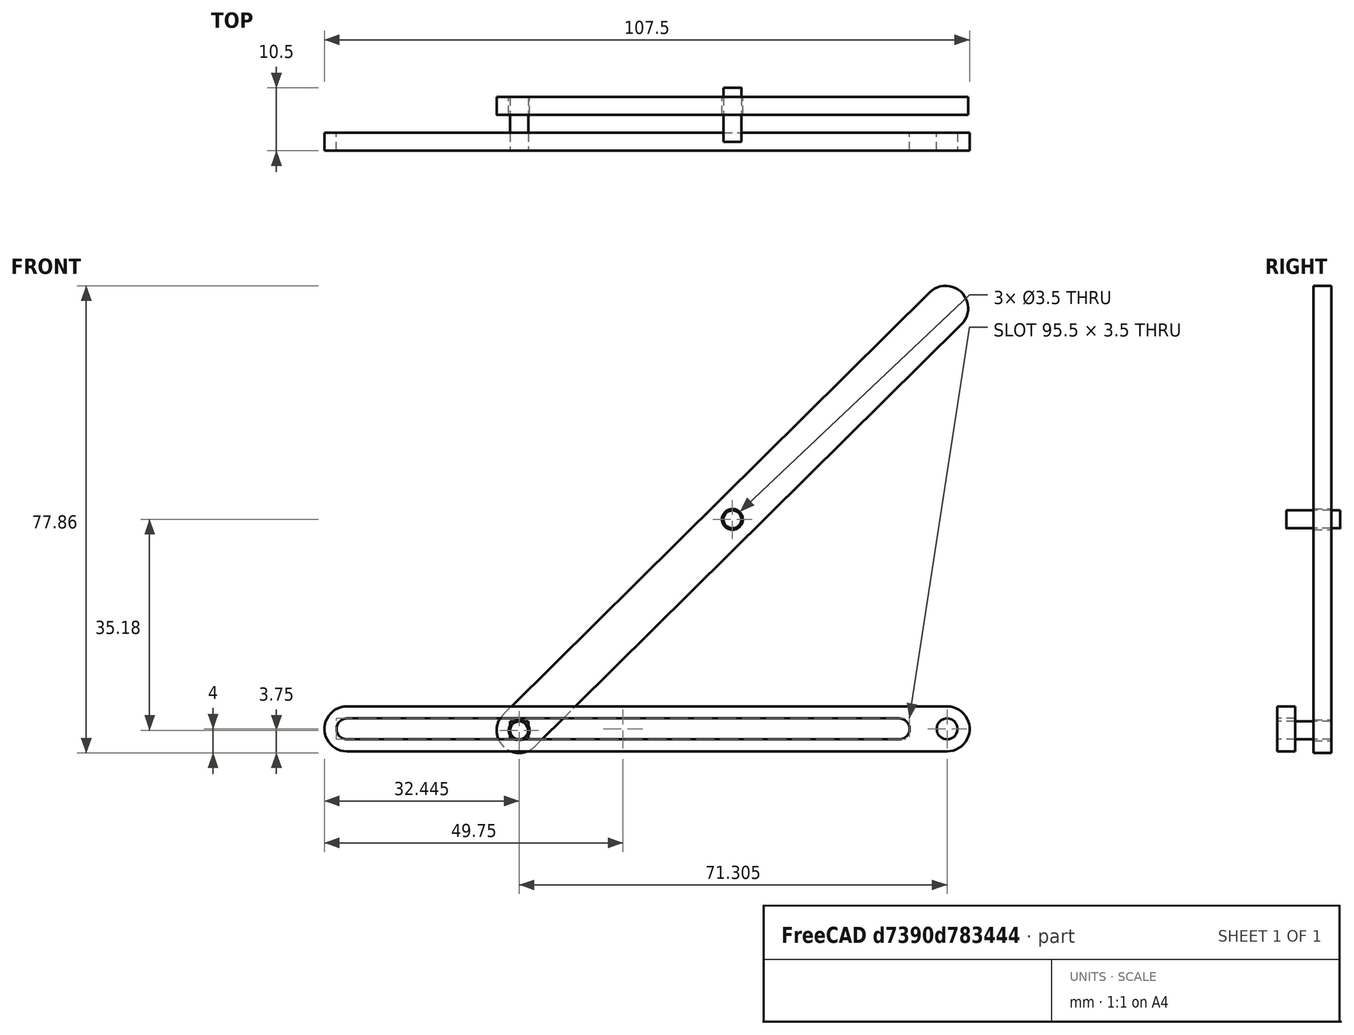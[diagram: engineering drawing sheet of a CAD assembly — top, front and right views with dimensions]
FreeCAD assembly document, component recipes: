
FREECAD ASSEMBLY — COMPONENT RECIPES ("scissor_lift")

This assembly document has 7 components, labeled P0..P6 below (a component is one placed body or linked part). 7 of them carry a construction recipe — the FreeCAD feature program that regenerates the part from scratch, quoted from this document or its linked companion documents; the rest are supplied as boundary geometry only. No exploded tour is included for this assembly.
COMPONENT P0 — recipe-attached ("base", modeled in this document).
Construction recipe (the document's own serialized feature program — sketch geometry with constraints, then the solid features built on it; lengths are millimeters unless a unit is written):

FEATURE [Sketcher::SketchObject] Sketch
  ArcFitTolerance = 1e-06
  AttachmentSupport = -> [XY_Plane]
  FullyConstrained = true
  MakeInternals = false
  MapMode = 5
  sketch-geometry (9):
    g0: ArcOfCircle CenterX=-50 CenterY=2e-16 CenterZ=0 NormalX=0 NormalY=0 NormalZ=1 AngleXU=0 Radius=3.75 StartAngle=1.5708 EndAngle=4.71239
    g1: ArcOfCircle CenterX=50 CenterY=-2e-16 CenterZ=0 NormalX=0 NormalY=0 NormalZ=1 AngleXU=0 Radius=3.75 StartAngle=4.71239 EndAngle=7.85398
    g2: LineSegment StartX=-50 StartY=3.75 StartZ=0 EndX=50 EndY=3.75 EndZ=0
    g3: LineSegment StartX=-50 StartY=-3.75 StartZ=0 EndX=50 EndY=-3.75 EndZ=0
    g4: ArcOfCircle CenterX=-50 CenterY=2e-16 CenterZ=0 NormalX=0 NormalY=0 NormalZ=1 AngleXU=0 Radius=1.75 StartAngle=1.5708 EndAngle=4.71239
    g5: ArcOfCircle CenterX=42 CenterY=3e-16 CenterZ=0 NormalX=0 NormalY=0 NormalZ=1 AngleXU=0 Radius=1.75 StartAngle=4.71239 EndAngle=7.85398
    g6: LineSegment StartX=-50 StartY=1.75 StartZ=0 EndX=42 EndY=1.75 EndZ=0
    g7: LineSegment StartX=-50 StartY=-1.75 StartZ=0 EndX=42 EndY=-1.75 EndZ=0
    g8: Circle CenterX=50 CenterY=-2e-16 CenterZ=0 NormalX=0 NormalY=0 NormalZ=1 AngleXU=0 Radius=1.75
  constraints (20):
    c: Tangent(g0,g2) = 1.5708
    c: Tangent(g0,g3) = -1.5708
    c: Tangent(g1,g2) = 1.5708
    c: Tangent(g1,g3) = -1.5708
    c: Equal(g0,g1)
    c: Horizontal(g3)
    c: Symmetric(g0,g1,g-1)
    c: DistanceX(g0,g1) = 100
    c: DistanceY(g0,g0) = 7.5
    c: Tangent(g4,g6) = 1.5708
    c: Tangent(g4,g7) = -1.5708
    c: Tangent(g5,g6) = 1.5708
    c: Tangent(g5,g7) = -1.5708
    c: Equal(g4,g5)
    c: Horizontal(g7)
    c: Distance(g4,g4) = 3.5
    c: Coincident(g8,g1)
    c: Diameter(g8) = 3.5
    c: DistanceX(g5,g1) = 8
    c: Coincident(g4,g0)
FEATURE [PartDesign::Pad] Pad
  Direction = (0,0,1)
  Length = 3
  Length2 = 10
  Profile = -> Sketch
  ReferenceAxis = -> Sketch [N_Axis]
  Refine = true
  Suppressed = false
  Type = 0
FEATURE [PartDesign::Body] Body  label="base"
  AllowCompound = false
  Group = -> [Sketch,Pad]
  Origin = -> Origin
  Placement = pos=(0,1.5,1.5) rot=(1,0,0;1.5708rad)
  Tip = -> Pad
COMPONENT P1 — recipe-attached ("arm_1", modeled in this document).
Construction recipe (the document's own serialized feature program — sketch geometry with constraints, then the solid features built on it; lengths are millimeters unless a unit is written):

FEATURE [PartDesign::SubShapeBinder] Binder
  BindCopyOnChange = 0
  BindMode = 0
  ClaimChildren = false
  Context = -> Assembly [Body001.Binder.]
  Fuse = false
  MakeFace = true
  OffsetFill = false
  OffsetIntersection = false
  OffsetJoinType = 0
  OffsetOpenResult = false
  PartialLoad = false
  Refine = true
  Relative = true
  Support = -> [Body]
  _Version = 2
FEATURE [Sketcher::SketchObject] Sketch001
  ArcFitTolerance = 1e-06
  AttachmentSupport = -> [XY_Plane001]
  ExternalGeometry = -> [Binder]
  FullyConstrained = true
  MakeInternals = false
  MapMode = 5
  sketch-geometry (6):
    g0: ArcOfCircle CenterX=-50 CenterY=1e-16 CenterZ=0 NormalX=0 NormalY=0 NormalZ=1 AngleXU=0 Radius=3.75 StartAngle=1.5708 EndAngle=4.71239
    g1: ArcOfCircle CenterX=50 CenterY=-1e-16 CenterZ=0 NormalX=0 NormalY=0 NormalZ=1 AngleXU=0 Radius=3.75 StartAngle=4.71239 EndAngle=7.85398
    g2: LineSegment StartX=-50 StartY=3.75 StartZ=0 EndX=50 EndY=3.75 EndZ=0
    g3: LineSegment StartX=-50 StartY=-3.75 StartZ=0 EndX=50 EndY=-3.75 EndZ=0
    g4: Circle CenterX=-50 CenterY=1e-16 CenterZ=0 NormalX=0 NormalY=0 NormalZ=1 AngleXU=0 Radius=1.75
    g5: Circle CenterX=0 CenterY=0 CenterZ=0 NormalX=0 NormalY=0 NormalZ=1 AngleXU=0 Radius=1.75
  constraints (13):
    c: Tangent(g0,g2) = 1.5708
    c: Tangent(g0,g3) = -1.5708
    c: Tangent(g1,g2) = 1.5708
    c: Tangent(g1,g3) = -1.5708
    c: Equal(g0,g1)
    c: Horizontal(g2)
    c: Symmetric(g0,g1,g-1)
    c: Equal(g2,g-3)
    c: Equal(g1,g-4)
    c: Coincident(g4,g0)
    c: Equal(g4,g-5)
    c: Coincident(g5,g-1)
    c: Equal(g5,g-5)
FEATURE [PartDesign::Pad] Pad001
  Direction = (0,0,1)
  Length = 3
  Length2 = 10
  Profile = -> Sketch001
  ReferenceAxis = -> Sketch001 [N_Axis]
  Refine = true
  Suppressed = false
  Type = 0
FEATURE [PartDesign::Body] Body001  label="arm_1"
  AllowCompound = false
  Group = -> [Binder,Sketch001,Pad001]
  Origin = -> Origin001
  Placement = pos=(14.2248,1.49999,36.4304) rot=(0.276713,0.679496,0.679496;3.68151rad)
  Tip = -> Pad001
COMPONENT P2 — recipe-attached ("arm_2", modeled in this document).
Construction recipe (the document's own serialized feature program — sketch geometry with constraints, then the solid features built on it; lengths are millimeters unless a unit is written):

FEATURE [PartDesign::FeatureBase] Clone
  BaseFeature = -> Body001
  Placement = pos=(0,14,0) rot=(0,0,1;0rad)
  Suppressed = false
FEATURE [PartDesign::Body] Body002  label="arm_2"
  AllowCompound = false
  Group = -> [Clone]
  Origin = -> Origin002
  Placement = pos=(24.0753,7.5,26.4822) rot=(0.864392,-0.355546,0.355546;1.71601rad)
  Tip = -> Clone
COMPONENT P3 — recipe-attached ("pin_1", modeled in this document).
Construction recipe (the document's own serialized feature program — sketch geometry with constraints, then the solid features built on it; lengths are millimeters unless a unit is written):

FEATURE [Sketcher::SketchObject] Sketch002
  ArcFitTolerance = 1e-06
  AttachmentSupport = -> [XY_Plane003]
  FullyConstrained = true
  MakeInternals = false
  MapMode = 5
  sketch-geometry (1):
    g0: Circle CenterX=0 CenterY=0 CenterZ=0 NormalX=0 NormalY=0 NormalZ=1 AngleXU=0 Radius=1.5
  constraints (2):
    c: Coincident(g0,g-1)
    c: Diameter(g0) = 3
FEATURE [PartDesign::Pad] Pad002
  Direction = (0,0,1)
  Length = 9
  Length2 = 10
  Profile = -> Sketch002
  ReferenceAxis = -> Sketch002 [N_Axis]
  Refine = true
  Suppressed = false
  Type = 0
FEATURE [PartDesign::Body] Body003  label="pin_1"
  AllowCompound = false
  Group = -> [Sketch002,Pad002]
  Origin = -> Origin003
  Placement = pos=(50,7.5,1.5) rot=(0.772485,0.449036,-0.449036;1.82612rad)
  Tip = -> Pad002
COMPONENT P4 — recipe-attached ("pin_2", modeled in this document).
Construction recipe (the document's own serialized feature program — sketch geometry with constraints, then the solid features built on it; lengths are millimeters unless a unit is written):

FEATURE [PartDesign::FeatureBase] Clone001
  BaseFeature = -> Body003
  Placement = pos=(-65,0,0) rot=(0,0,1;0rad)
  Suppressed = false
FEATURE [PartDesign::Body] Body004  label="pin_2"
  AllowCompound = false
  Group = -> [Clone001]
  Origin = -> Origin004
  Placement = pos=(58.3467,2.05569e-06,-11.3007) rot=(-0.850439,0.371991,0.371991;1.73209rad)
  Tip = -> Clone001
COMPONENT P5 — recipe-attached ("pin_3", modeled in this document).
Construction recipe (the document's own serialized feature program — sketch geometry with constraints, then the solid features built on it; lengths are millimeters unless a unit is written):

FEATURE [PartDesign::FeatureBase] Clone002
  BaseFeature = -> Body003
  Placement = pos=(-65,0,0) rot=(0,0,1;0rad)
  Suppressed = false
FEATURE [PartDesign::Body] Body005  label="pin_3"
  AllowCompound = false
  Group = -> [Clone002]
  Origin = -> Origin005
  Placement = pos=(15.1366,-1.50001,55.0741) rot=(-0.799856,-0.424399,-0.424399;1.79229rad)
  Tip = -> Clone002
COMPONENT P6 — recipe-attached ("constraint", modeled in this document).
Construction recipe (the document's own serialized feature program — sketch geometry with constraints, then the solid features built on it; lengths are millimeters unless a unit is written):

FEATURE [PartDesign::SubShapeBinder] Binder001
  BindCopyOnChange = 0
  BindMode = 0
  ClaimChildren = false
  Context = -> Assembly [Body006.Binder001.]
  Fuse = false
  MakeFace = true
  OffsetFill = false
  OffsetIntersection = false
  OffsetJoinType = 0
  OffsetOpenResult = false
  PartialLoad = false
  Refine = true
  Relative = true
  Support = -> [Body005]
  _Version = 2
FEATURE [Sketcher::SketchObject] Sketch003
  ArcFitTolerance = 1e-06
  AttachmentSupport = -> [XZ_Plane007]
  ExternalGeometry = -> [Binder001]
  FullyConstrained = false
  MakeInternals = false
  MapMode = 5
  Placement = pos=(0,0,0) rot=(1,0,0;1.5708rad)
  sketch-geometry (4):
    g0: LineSegment StartX=-36.1694 StartY=2.99185 StartZ=0 EndX=-36.1694 EndY=-0.00815282 EndZ=0
    g1: LineSegment StartX=-36.1694 StartY=-0.00815282 StartZ=0 EndX=-33.1694 EndY=-0.00815282 EndZ=0
    g2: LineSegment StartX=-33.1694 StartY=-0.00815282 StartZ=0 EndX=-33.1694 EndY=2.99185 EndZ=0
    g3: LineSegment StartX=-33.1694 StartY=2.99185 StartZ=0 EndX=-36.1694 EndY=2.99185 EndZ=0
  constraints (10):
    c: Coincident(g0,g1)
    c: Coincident(g1,g2)
    c: Coincident(g2,g3)
    c: Coincident(g3,g0)
    c: Vertical(g0)
    c: Vertical(g2)
    c: Horizontal(g1)
    c: Horizontal(g3)
    c: Equal(g3,g2)
    c: DistanceX(g3,g3) = 3
FEATURE [PartDesign::Pad] Pad003
  Direction = (0,-1,2e-16)
  Length = 3
  Length2 = 10
  Placement = pos=(0,0,0) rot=(1,0,0;1.5708rad)
  Profile = -> Sketch003
  ReferenceAxis = -> Sketch003 [N_Axis]
  Refine = true
  Suppressed = false
  Type = 0
FEATURE [PartDesign::Body] Body006  label="constraint"
  AllowCompound = false
  Group = -> [Sketch003,Binder001,Pad003]
  Origin = -> Origin007
  Placement = pos=(13.3648,1.5,-0.241847) rot=(0.99808,0,0;0rad)
  Tip = -> Pad003
PROVENANCE & LICENSES
A FreeCAD (.FCStd) document from a public repository crawl; recipes are the document's own serialized feature recipes (and, for linked parts, companion documents' recipes).
License: as declared in the source repository (recorded in the dataset sidecar).
